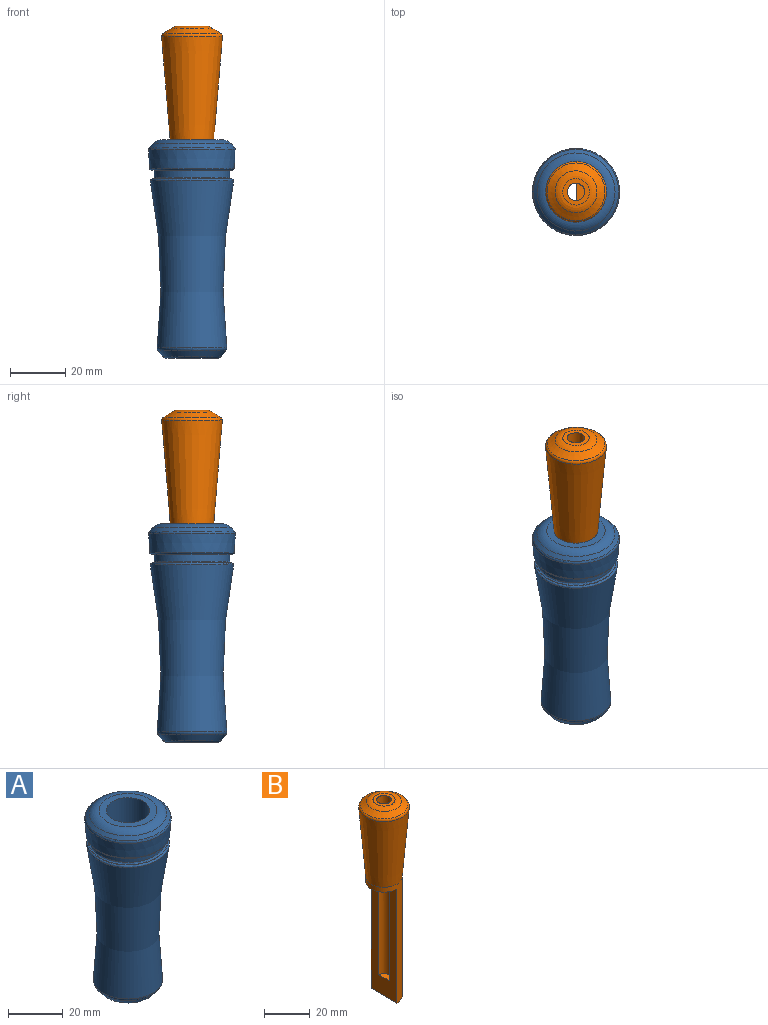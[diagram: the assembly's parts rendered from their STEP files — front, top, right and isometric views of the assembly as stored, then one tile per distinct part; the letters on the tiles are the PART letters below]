
ASSEMBLY  parts=2 mates=1
PART A: 18 faces, bbox 144.5x144.5x271.5 mm
  f0: plane 19.1x19.1mm, normal (0,0,-1), area 77mm2, adj f15,f17
  f1: plane 21.19x21.19mm, normal (0,0,1), area 154.8mm2, adj f9,f10
  f2: cone r=12.7mm half-angle=45deg, axis (0,0,-1), area 168mm2, adj f10,f11
  f3: cone r=15.88mm half-angle=4.3deg, axis (0,0,1), area 664.4mm2, adj f11,f12
  f4: plane 29.38x29.38mm, normal (0,0,-1), area 89mm2, adj f5,f12
  f5: cylinder r=13.69mm len=27.38mm, axis (0,0,1), area 218.5mm2, adj f4,f13
  f6: plane 29x29mm, normal (0,0,1), area 15.8mm2, adj f13,f14
  f7: torus R=202.53mm, axis (0,0,1), area 4696.6mm2, adj f14,f16
  f8: cone r=10.16mm half-angle=38.7deg, axis (0,0,1), area 210.4mm2, adj f16,f17
  f9: cylinder r=7.94mm len=79.15mm, axis (0,0,1), area 3947.3mm2, adj f1,f15
  f10: torus R=10.6mm, axis (0,0,1), area 313.1mm2, adj f1,f2
  f11: torus R=14.56mm, axis (0,0,-1), area 107.9mm2, adj f2,f3
  f12: torus R=14.69mm, axis (0,0,-1), area 90mm2, adj f3,f4
  f13: torus R=14.33mm, axis (0,0,-1), area 87.3mm2, adj f5,f6
  f14: torus R=14.5mm, axis (0,0,1), area 105.5mm2, adj f6,f7
  f15: torus R=8.17mm, axis (0,0,1), area 18.1mm2, adj f0,f9
  f16: torus R=11.38mm, axis (0,0,-1), area 79.5mm2, adj f7,f8
  f17: torus R=9.55mm, axis (0,0,1), area 72.1mm2, adj f0,f8
PART B: 11 faces, bbox 23.9x23.9x104.8 mm
  f0: plane 15.88x7.94mm, normal (0,0,-1), area 99mm2, adj f2,f5
  f1: cone r=7.94mm half-angle=4.8deg, axis (0,0,1), area 2235.9mm2, adj f2,f10
  f2: cylinder r=7.94mm len=63.5mm, axis (0,0,-1), area 1646.8mm2, adj f0,f1,f5,f6
  f3: plane 9.62x9.62mm, normal (0,0,1), area 41.1mm2, adj f7,f9
  f4: cone r=11.11mm half-angle=56.3deg, axis (0,0,-1), area 195.6mm2, adj f9,f10
  f5: plane 60.96x15.88mm, normal (-1,0,0), area 641.1mm2, adj f0,f2,f6,f7,f8
  f6: plane 15.88x7.94mm, normal (0,0,-1), area 83.1mm2, adj f2,f5,f7
  f7: cylinder r=3.17mm len=95.25mm, axis (0,0,1), area 1387.1mm2, adj f3,f5,f6,f8
  f8: plane 6.35x3.18mm, normal (0,0,1), area 15.8mm2, adj f5,f7
  f9: torus R=4.81mm, axis (0,0,-1), area 117.5mm2, adj f3,f4
  f10: torus R=9.78mm, axis (0,0,1), area 92.5mm2, adj f1,f4
PLACE A at identity
PLACE B t=(-45.68,0,0)mm
MATE revolute B.f1 <-> A.f2  axis (0,0,-1) through (-31.83,0,0)mm
